# Revit family: 3328ST026_065
name_source: partatom
category: Plumbing Fixtures
revit_build: Autodesk Revit Architecture 2012 (Build: 20110309_2315(x64)
units: mm (PartAtom-declared; Revit-internal decimal feet)

## types (1)
- 3328ST026/065
    1/2" light pattern tap washer = C-098-15
    Assembly Code = D2010
    CW Connection = Yes
    CWFU = 0
    Cost = 0 $
    Default Elevation = 0' - 0"
    Description = 2 x undertile stoptaps with 1/2"BSP female inlets + shower arm + rose
    HW Connection = Yes
    HWFU = 0
    Keynote = 2 x Stella stoptaps complete
    Manufacturer = COBRA
    Material = Chrome - Polished
    Model = 3328ST026/065
    Range = Stella
    Shower arm = 026
    Shower head = 065
    Stoptap sliding wall flange = C-FL30X1
    Tap handle = C-HA29X1
    Tap headpart complete = P-63-2ST
    Type Comments = SANS 226 TYPE 2
    Vent Connection = No
    WFU = 0
    Waste Connection = No

## geometry (parser evidence)
native form markers: Blend x3
no freeform markers — native parametric forms only
